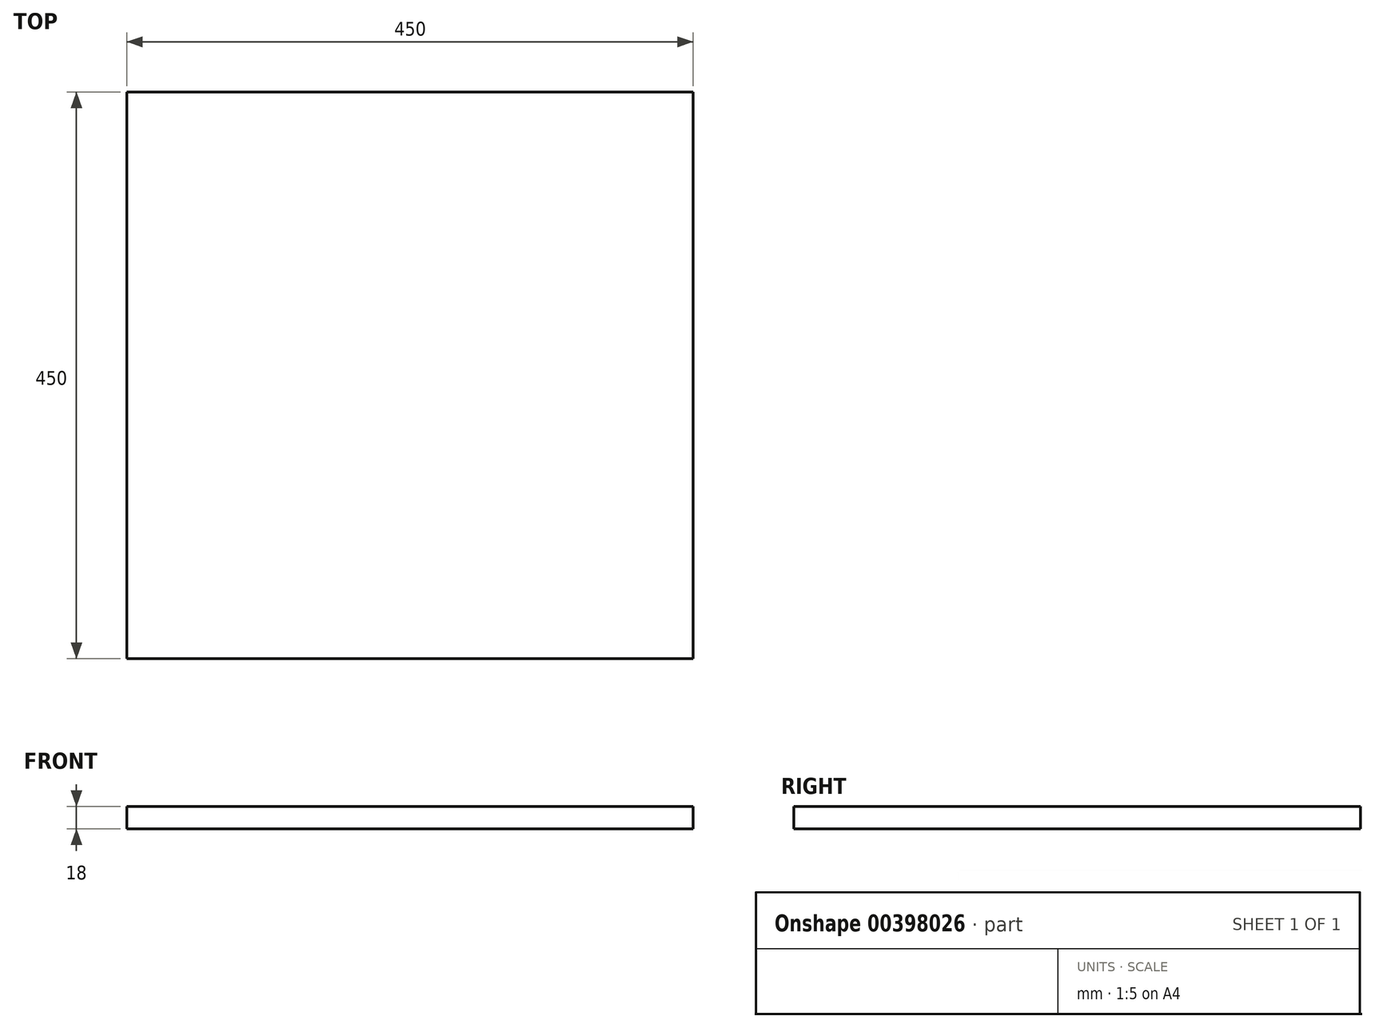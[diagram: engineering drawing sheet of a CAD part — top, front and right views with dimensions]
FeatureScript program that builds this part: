
annotation { "Feature Type Name" : "Feature", "Feature Type Description" : "" }
export const myFeature = defineFeature(function(context is Context, id is Id, definition is map)
    precondition{}
    {
        {
            var Q0;
            Q0=qCreatedBy(makeId("Top.planeOp"),FACE);
            var sketch = newSketch(context, id + "F0", { "sketchPlane" : qUnion([Q0])});
            skLineSegment(sketch, "E0.bottom", {"start": v(225, -225) * mm, "end": v(-225, -225) * mm});
            skLineSegment(sketch, "E0.top", {"start": v(225, 225) * mm, "end": v(-225, 225) * mm});
            skLineSegment(sketch, "E0.left", {"start": v(225, -225) * mm, "end": v(225, 225) * mm});
            skLineSegment(sketch, "E0.right", {"start": v(-225, -225) * mm, "end": v(-225, 225) * mm});
            skPoint(sketch, "E0.middle", {"position": v(0, 0) * mm});
            skSolve(sketch);
        }
        {
            var Q0;
            Q0 = qSketchRegion(id + "F0", true);
            extrude(context, id + "F1", {"entities" : qUnion([Q0]), "depth" : 18 * mm});
        }
    });
